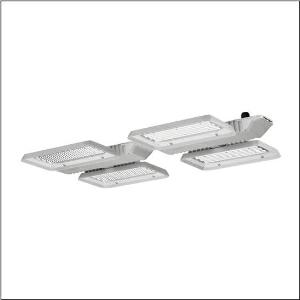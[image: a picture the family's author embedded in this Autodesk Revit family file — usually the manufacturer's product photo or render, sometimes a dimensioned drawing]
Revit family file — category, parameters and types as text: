
# Revit family: highbay_11_51hla2d24nca
name_source: partatom
category: Lighting Fixtures
units: mm (PartAtom-declared; Revit-internal decimal feet)

## family parameters
Cut with Voids When Loaded = No
Host = Face
Light Source = No
Part Type = Normal
Room Calculation Point = No
Round Connector Dimension = Use Diameter
Shared = No

## types (1)
- --- (1 x LED, 33150 lm, 189.6 W, 4000K)
    Apparent Load = 190 VA
    CIE Flux Codes = 89 96 99 100 100
    Color Rendering = 80
    Color Temperature = 4000K
    Default Elevation = 1800 mm
    Description = Highbay 11, LED high bay luminaire, primary light control with lens, of PMMA, light emission: direct distribution, primary light characteristic: symmetric, installation type: surface-mounted, suspended mounting, for 2x 2x LED, rated luminous flux: 33.150lm, luminous efficacy: 175lm/W, light colour: 840, colour temperature: 4000K, control gear: DALI (with two DALI addresses), with terminal, 5-pole, max. 2.5mm², mains connection: 230..240V, AC, 50/60Hz, rated input power: 190W, LED unit, of diecast aluminium, unplated, bead blasted, silver, length: 940mm, width: 500mm, height: 65mm, housing, of diecast aluminium, uncoated, bead blasted, silver, protection rating (complete): IP65, insulation class (complete): insulation class I (protective earthing), certification: CE, ENEC, VDE, UKCA, protection symbol: D, impact resistance: IK08 with glass or PC cover, permissible operating ambient temperature: -35..+45°C, reducing of maximum allowable ambient temperature of 5°C with ceiling mounting, corresponds to IFS (International Featured Standards) requirements for safety and quality in the food industry, packaging unit: 1 piece
    Height = 95 mm
    Lamp = 1 x LED
    Lamp Light Flux = 33150 lm
    Lamp Power = 189.6 W
    Lamp count = 1
    Length = 939 mm
    Luminous efficacy = 175 lm/W
    Manufacturer = Siteco
    ModVariant = No
    Model = 51HLA2D24NCA
    Mounting Place = Ceiling
    Mounting Type = Pendant
    Number of Poles = 1
    OnlyDefault = Yes
    Power Factor = 1
    Product Name = Highbay 11
    Product group = LED high bay luminaire
    ProductGroupID = 903
    Protection Class = Protection class I
    Protection Degree = IP 65
    RLX_Detail_Level = 1
    RLX_Emergency_Light_Flux = 0 lm
    RLX_Emergency_Type = 0
    RLX_Emergency_Type_DB = No
    RlxData = <blob elided: 97193 chars, md5=7835379b>
    Socket = socket
    Standby Power = 0 W
    System Light Flux = 33150 lm
    System Power = 190 W
    Type Comments = factory setting: luminous flux: 100 % | dim-lin: 254 | 535 mA
    Type Image = l_1003428.jpg
    URL = http://relux.com
    VarID = @adj_201354
    Voltage = 0 V
    Weight = 0.00 kg
    Width = 501 mm

## geometry (parser evidence)
native form markers: Blend x4, Sweep x12
no freeform markers — native parametric forms only
